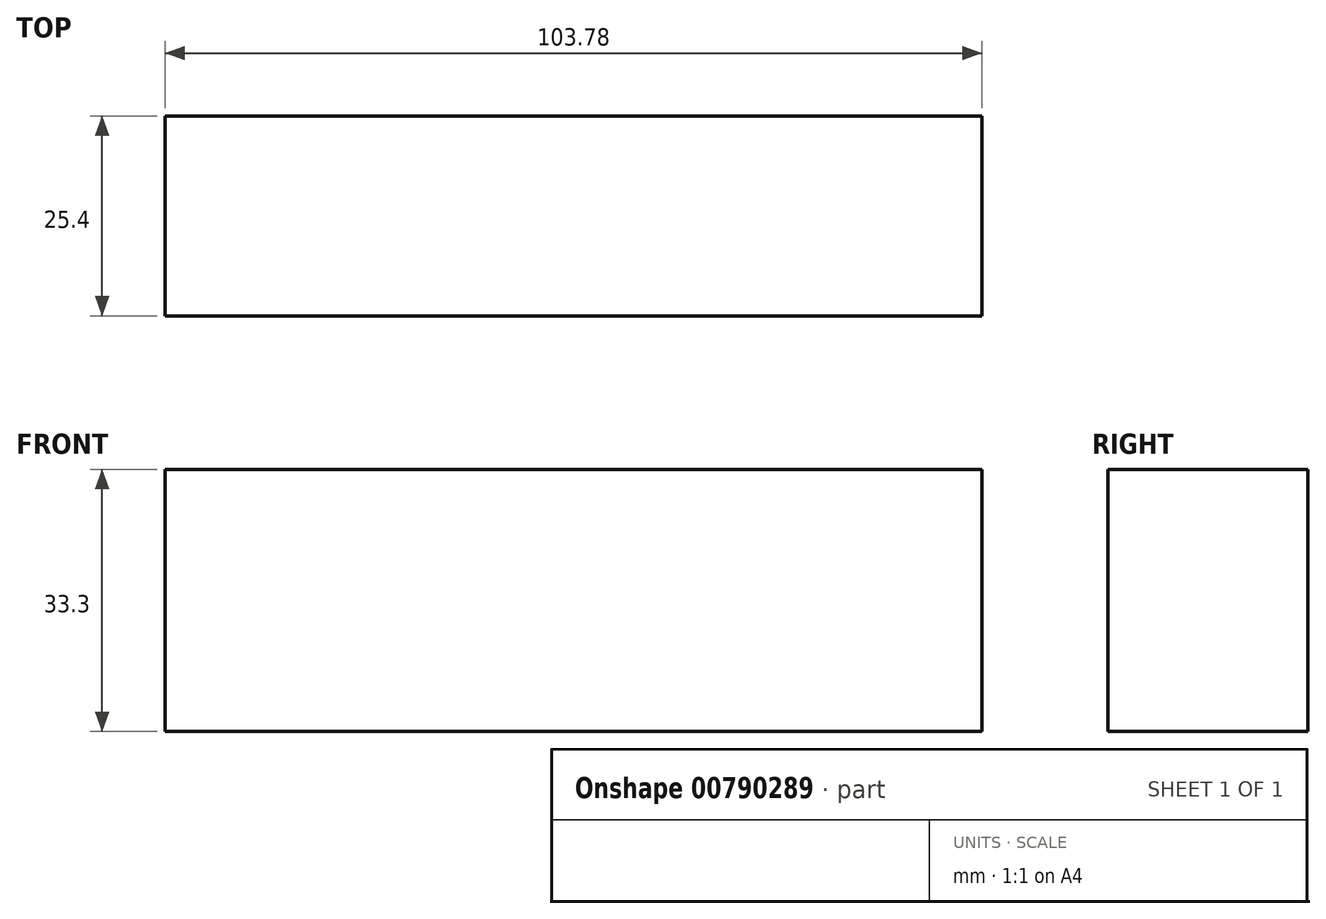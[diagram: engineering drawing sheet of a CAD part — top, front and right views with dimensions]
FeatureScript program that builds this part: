
annotation { "Feature Type Name" : "Feature", "Feature Type Description" : "" }
export const myFeature = defineFeature(function(context is Context, id is Id, definition is map)
    precondition{}
    {
        {
            var Q0;
            Q0=qCreatedBy(makeId("Front.planeOp"),FACE);
            var sketch = newSketch(context, id + "F0", { "sketchPlane" : qUnion([Q0])});
            skLineSegment(sketch, "E0.bottom", {"start": v(-38.64, 6.48) * mm, "end": v(65.14, 6.48) * mm});
            skLineSegment(sketch, "E0.top", {"start": v(-38.64, 39.78) * mm, "end": v(65.14, 39.78) * mm});
            skLineSegment(sketch, "E0.left", {"start": v(-38.64, 6.48) * mm, "end": v(-38.64, 39.78) * mm});
            skLineSegment(sketch, "E0.right", {"start": v(65.14, 6.48) * mm, "end": v(65.14, 39.78) * mm});
            skPoint(sketch, "E1.orphan", {"position": v(-38.64, 23.13) * mm});
            skPoint(sketch, "E2.end.orphan", {"position": v(65.14, 23.13) * mm});
            skPoint(sketch, "E3.start.orphan", {"position": v(0, 39.78) * mm});
            skPoint(sketch, "E4.end.orphan", {"position": v(13.25, 6.48) * mm});
            skPoint(sketch, "E4.start.orphan", {"position": v(13.25, 39.78) * mm});
            skSolve(sketch);
        }
        {
            var Q0;
            {var subQ0=sQuery(id+"F0.wireOp",EDGE,"E0.left");var subQ1=sQuery(id+"F0.wireOp",EDGE,"E0.top");var subQ2=makeQuery(id+"F0.imprint","INTERSECT",VERTEX,{"derivedFrom":[subQ1,subQ0]});Q0=makeQuery(id+"F0.imprint","IMPRINT",FACE,{"disambiguationData":[TD([[makeQuery(id+"F0.imprint","IMPRINT",EDGE,{"disambiguationData":[TD([[subQ2,-1.0]])],"derivedFrom":subQ1}),-1.0]])]});}
            var Q1;
            {var subQ0=sQuery(id+"F0.wireOp",EDGE,"E0.right");var subQ1=sQuery(id+"F0.wireOp",EDGE,"E0.bottom");var subQ2=makeQuery(id+"F0.imprint","INTERSECT",VERTEX,{"derivedFrom":[subQ1,subQ0]});Q1=makeQuery(id+"F0.imprint","IMPRINT",FACE,{"disambiguationData":[TD([[makeQuery(id+"F0.imprint","IMPRINT",EDGE,{"disambiguationData":[TD([[subQ2,1.0]])],"derivedFrom":subQ1}),1.0]])]});}
            var Q2;
            {var subQ0=sQuery(id+"F0.wireOp",EDGE,"E0.left");var subQ1=sQuery(id+"F0.wireOp",EDGE,"E0.bottom");var subQ2=makeQuery(id+"F0.imprint","INTERSECT",VERTEX,{"derivedFrom":[subQ1,subQ0]});Q2=makeQuery(id+"F0.imprint","IMPRINT",FACE,{"disambiguationData":[TD([[makeQuery(id+"F0.imprint","IMPRINT",EDGE,{"disambiguationData":[TD([[subQ2,-1.0]])],"derivedFrom":subQ1}),1.0]])]});}
            var Q3;
            {var subQ0=sQuery(id+"F0.wireOp",EDGE,"E0.right");var subQ1=sQuery(id+"F0.wireOp",EDGE,"E0.top");var subQ2=makeQuery(id+"F0.imprint","INTERSECT",VERTEX,{"derivedFrom":[subQ1,subQ0]});Q3=makeQuery(id+"F0.imprint","IMPRINT",FACE,{"disambiguationData":[TD([[makeQuery(id+"F0.imprint","IMPRINT",EDGE,{"disambiguationData":[TD([[subQ2,1.0]])],"derivedFrom":subQ1}),-1.0]])]});}
            var Q4;
            {var subQ0=sQuery(id+"F0.wireOp",EDGE,"lJ0TX5be-G6iX-oMxm-q0rY-Al5fYiLwSnbA");var subQ1=sQuery(id+"F0.wireOp",EDGE,"E0.bottom");var subQ2=makeQuery(id+"F0.imprint","INTERSECT",VERTEX,{"derivedFrom":[subQ1,subQ0]});Q4=makeQuery(id+"F0.imprint","IMPRINT",FACE,{"disambiguationData":[TD([[makeQuery(id+"F0.imprint","IMPRINT",EDGE,{"disambiguationData":[TD([[subQ2,-1.0]])],"derivedFrom":subQ1}),1.0]])]});}
            var Q5;
            {var subQ0=sQuery(id+"F0.wireOp",EDGE,"hFb2d1FR-BCCz-fbbn-J8Fg-5DCYAxr15fKq");var subQ1=sQuery(id+"F0.wireOp",EDGE,"E0.bottom");var subQ2=makeQuery(id+"F0.imprint","INTERSECT",VERTEX,{"derivedFrom":[subQ1,subQ0]});Q5=makeQuery(id+"F0.imprint","IMPRINT",FACE,{"disambiguationData":[TD([[makeQuery(id+"F0.imprint","IMPRINT",EDGE,{"disambiguationData":[TD([[subQ2,-1.0]])],"derivedFrom":subQ1}),1.0]])]});}
            var Q6;
            {var subQ0=sQuery(id+"F0.wireOp",EDGE,"M7ohUQYM-nhFk-P8sq-LQ7H-sWNCLgzpDy4x");var subQ1=sQuery(id+"F0.wireOp",EDGE,"E0.bottom");var subQ2=makeQuery(id+"F0.imprint","INTERSECT",VERTEX,{"derivedFrom":[subQ1,subQ0]});Q6=makeQuery(id+"F0.imprint","IMPRINT",FACE,{"disambiguationData":[TD([[makeQuery(id+"F0.imprint","IMPRINT",EDGE,{"disambiguationData":[TD([[subQ2,-1.0]])],"derivedFrom":subQ1}),1.0]])]});}
            var Q7;
            {var subQ0=sQuery(id+"F0.wireOp",EDGE,"E3");var subQ1=sQuery(id+"F0.wireOp",EDGE,"E0.bottom");var subQ2=makeQuery(id+"F0.imprint","INTERSECT",VERTEX,{"derivedFrom":[subQ1,subQ0]});Q7=makeQuery(id+"F0.imprint","IMPRINT",FACE,{"disambiguationData":[TD([[makeQuery(id+"F0.imprint","IMPRINT",EDGE,{"disambiguationData":[TD([[subQ2,-1.0]])],"derivedFrom":subQ1}),1.0]])]});}
            var Q8;
            {var subQ0=sQuery(id+"F0.wireOp",EDGE,"lJ0TX5be-G6iX-oMxm-q0rY-Al5fYiLwSnbA");var subQ1=sQuery(id+"F0.wireOp",EDGE,"E0.top");var subQ2=makeQuery(id+"F0.imprint","INTERSECT",VERTEX,{"derivedFrom":[subQ1,subQ0]});Q8=makeQuery(id+"F0.imprint","IMPRINT",FACE,{"disambiguationData":[TD([[makeQuery(id+"F0.imprint","IMPRINT",EDGE,{"disambiguationData":[TD([[subQ2,-1.0]])],"derivedFrom":subQ1}),-1.0]])]});}
            var Q9;
            {var subQ0=sQuery(id+"F0.wireOp",EDGE,"hFb2d1FR-BCCz-fbbn-J8Fg-5DCYAxr15fKq");var subQ1=sQuery(id+"F0.wireOp",EDGE,"E0.top");var subQ2=makeQuery(id+"F0.imprint","INTERSECT",VERTEX,{"derivedFrom":[subQ1,subQ0]});Q9=makeQuery(id+"F0.imprint","IMPRINT",FACE,{"disambiguationData":[TD([[makeQuery(id+"F0.imprint","IMPRINT",EDGE,{"disambiguationData":[TD([[subQ2,-1.0]])],"derivedFrom":subQ1}),-1.0]])]});}
            var Q10;
            {var subQ0=sQuery(id+"F0.wireOp",EDGE,"M7ohUQYM-nhFk-P8sq-LQ7H-sWNCLgzpDy4x");var subQ1=sQuery(id+"F0.wireOp",EDGE,"E0.top");var subQ2=makeQuery(id+"F0.imprint","INTERSECT",VERTEX,{"derivedFrom":[subQ1,subQ0]});Q10=makeQuery(id+"F0.imprint","IMPRINT",FACE,{"disambiguationData":[TD([[makeQuery(id+"F0.imprint","IMPRINT",EDGE,{"disambiguationData":[TD([[subQ2,-1.0]])],"derivedFrom":subQ1}),-1.0]])]});}
            var Q11;
            {var subQ0=sQuery(id+"F0.wireOp",EDGE,"E3");var subQ1=sQuery(id+"F0.wireOp",EDGE,"E0.top");var subQ2=makeQuery(id+"F0.imprint","INTERSECT",VERTEX,{"derivedFrom":[subQ1,subQ0]});Q11=makeQuery(id+"F0.imprint","IMPRINT",FACE,{"disambiguationData":[TD([[makeQuery(id+"F0.imprint","IMPRINT",EDGE,{"disambiguationData":[TD([[subQ2,-1.0]])],"derivedFrom":subQ1}),-1.0]])]});}
            extrude(context, id + "F1", {"entities" : qUnion([Q0, Q1, Q2, Q3, Q4, Q5, Q6, Q7, Q8, Q9, Q10, Q11]), "depth" : 25.4 * mm, "offsetDistance" : 25.4 * mm});
        }
    });
